# Revit family: Zumtobel MIREL-L A L1200
name_source: partatom
category: Lighting Fixtures
revit_build: Autodesk Revit 2014 (Build: 20140709_2115(x64)
units: mm (PartAtom-declared; Revit-internal decimal feet)

## types (3) — shared parameters
Assembly Code = D5020200
Color Filter = 16777215
Description = Surface mount LED luminaire
Dimming Lamp Color Temperature Shift = <None>
Emit Shape Visible in Rendering = No
Emit from Rectangle Length = 300 mm  [stored 0.984252 ft]
Emit from Rectangle Width = 1200 mm  [stored 3.93701 ft]
Height = 52 mm
Lamp = LED
Length = 1200 mm  [stored 3.93701 ft]
Manufacturer = Zumtobel Lighting
Tilt Angle = 90.00°
URL = http://www.zumtobel.com
Voltage = 230 V
Width = 300 mm  [stored 0.984252 ft]
zero-valued in all types: Default Elevation

## per-type parameters (varying)
| type | Apparent Load | Model | Photometric Web File |
| MIREL-L A LED840 L1200 EVG | 37 VA | 42182128 | 42182128_(STD).IES |
| MIREL-L A LED840 L1200 LDO | 38 VA | 42925615 | 42925615_(STD).IES |
| MIREL-L A LED840 L1200 EVG TEC | 28 VA | 42183096 | 42183096_(STD).IES |

note: [stored X ft] marks values corroborated as IEEE doubles in the binary element streams (Revit-internal decimal feet)

## geometry (parser evidence)
native form markers: Sweep x2
no freeform markers — native parametric forms only
